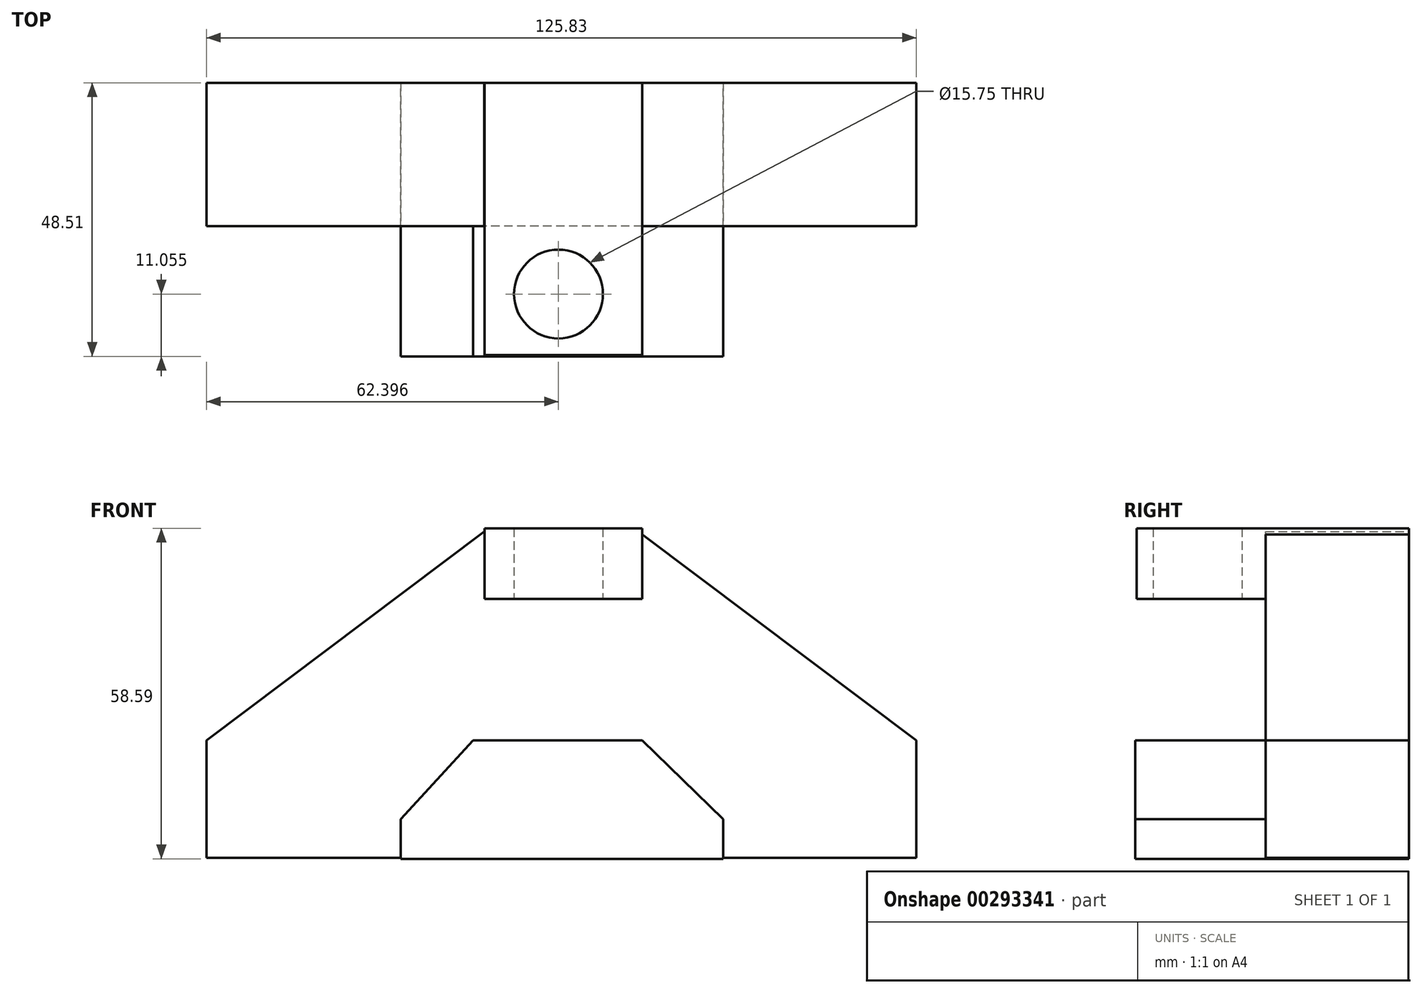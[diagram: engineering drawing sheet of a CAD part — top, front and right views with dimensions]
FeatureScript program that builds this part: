
annotation { "Feature Type Name" : "Feature", "Feature Type Description" : "" }
export const myFeature = defineFeature(function(context is Context, id is Id, definition is map)
    precondition{}
    {
        {
            var Q0;
            Q0=qCreatedBy(makeId("Front.planeOp"),FACE);
            var sketch = newSketch(context, id + "F0", { "sketchPlane" : qUnion([Q0])});
            skLineSegment(sketch, "E0", {"start": v(-43.1, 8.32) * mm, "end": v(-43.1, -12.5) * mm});
            skLineSegment(sketch, "E1", {"start": v(-43.1, -12.5) * mm, "end": v(82.73, -12.5) * mm});
            skLineSegment(sketch, "E2", {"start": v(82.73, -12.5) * mm, "end": v(82.73, 8.32) * mm});
            skLineSegment(sketch, "E3", {"start": v(-43.1, 8.32) * mm, "end": v(6.12, 45.32) * mm});
            skLineSegment(sketch, "E4", {"start": v(6.12, 45.32) * mm, "end": v(33.52, 45.32) * mm});
            skLineSegment(sketch, "E5", {"start": v(33.52, 45.32) * mm, "end": v(82.73, 8.32) * mm});
            skSolve(sketch);
        }
        {
            var Q0;
            Q0 = qSketchRegion(id + "F0", true);
            extrude(context, id + "F1", {"entities" : qUnion([Q0]), "depth" : 25.4 * mm});
        }
        {
            var Q0;
            Q0=qCreatedBy(makeId("Front.planeOp"),FACE);
            var sketch = newSketch(context, id + "F2", { "sketchPlane" : qUnion([Q0])});
            skLineSegment(sketch, "E6.bottom", {"start": v(6.18, 45.9) * mm, "end": v(34.16, 45.9) * mm});
            skLineSegment(sketch, "E6.top", {"start": v(6.18, 33.37) * mm, "end": v(34.16, 33.37) * mm});
            skLineSegment(sketch, "E6.left", {"start": v(6.18, 45.9) * mm, "end": v(6.18, 33.37) * mm});
            skLineSegment(sketch, "E6.right", {"start": v(34.16, 45.9) * mm, "end": v(34.16, 33.37) * mm});
            skSolve(sketch);
        }
        {
            var Q0;
            Q0 = qSketchRegion(id + "F2", true);
            extrude(context, id + "F3", {"entities" : qUnion([Q0]), "operationType" : NewBodyOperationType.ADD, "depth" : 48.26 * mm});
        }
        {
            var Q0;
            Q0=qCreatedBy(makeId("Top.planeOp"),FACE);
            var sketch = newSketch(context, id + "F4", { "sketchPlane" : qUnion([Q0])});
            skCircle(sketch, "E7", {"center": v(19.3, -37.45) * mm, "radius": 7.87 * mm});
            skSolve(sketch);
        }
        {
            var Q0;
            Q0 = qSketchRegion(id + "F4", true);
            extrude(context, id + "F5", {"entities" : qUnion([Q0]), "operationType" : NewBodyOperationType.REMOVE, "depth" : 52.32 * mm});
        }
        {
            var Q0;
            Q0=qCreatedBy(makeId("Front.planeOp"),FACE);
            var sketch = newSketch(context, id + "F6", { "sketchPlane" : qUnion([Q0])});
            skLineSegment(sketch, "E8", {"start": v(-8.7, -12.68) * mm, "end": v(48.45, -12.68) * mm});
            skLineSegment(sketch, "E9", {"start": v(-8.7, -12.68) * mm, "end": v(-8.7, -5.68) * mm});
            skLineSegment(sketch, "E10", {"start": v(48.45, -12.68) * mm, "end": v(48.45, -5.68) * mm});
            skLineSegment(sketch, "E11", {"start": v(4.14, 8.34) * mm, "end": v(-8.7, -5.68) * mm});
            skLineSegment(sketch, "E12", {"start": v(4.14, 8.34) * mm, "end": v(34.16, 8.34) * mm});
            skLineSegment(sketch, "E13", {"start": v(34.16, 8.34) * mm, "end": v(48.45, -5.68) * mm});
            skSolve(sketch);
        }
        {
            var Q0;
            Q0 = qSketchRegion(id + "F6", true);
            extrude(context, id + "F7", {"entities" : qUnion([Q0]), "operationType" : NewBodyOperationType.ADD, "depth" : 48.5 * mm});
        }
    });
